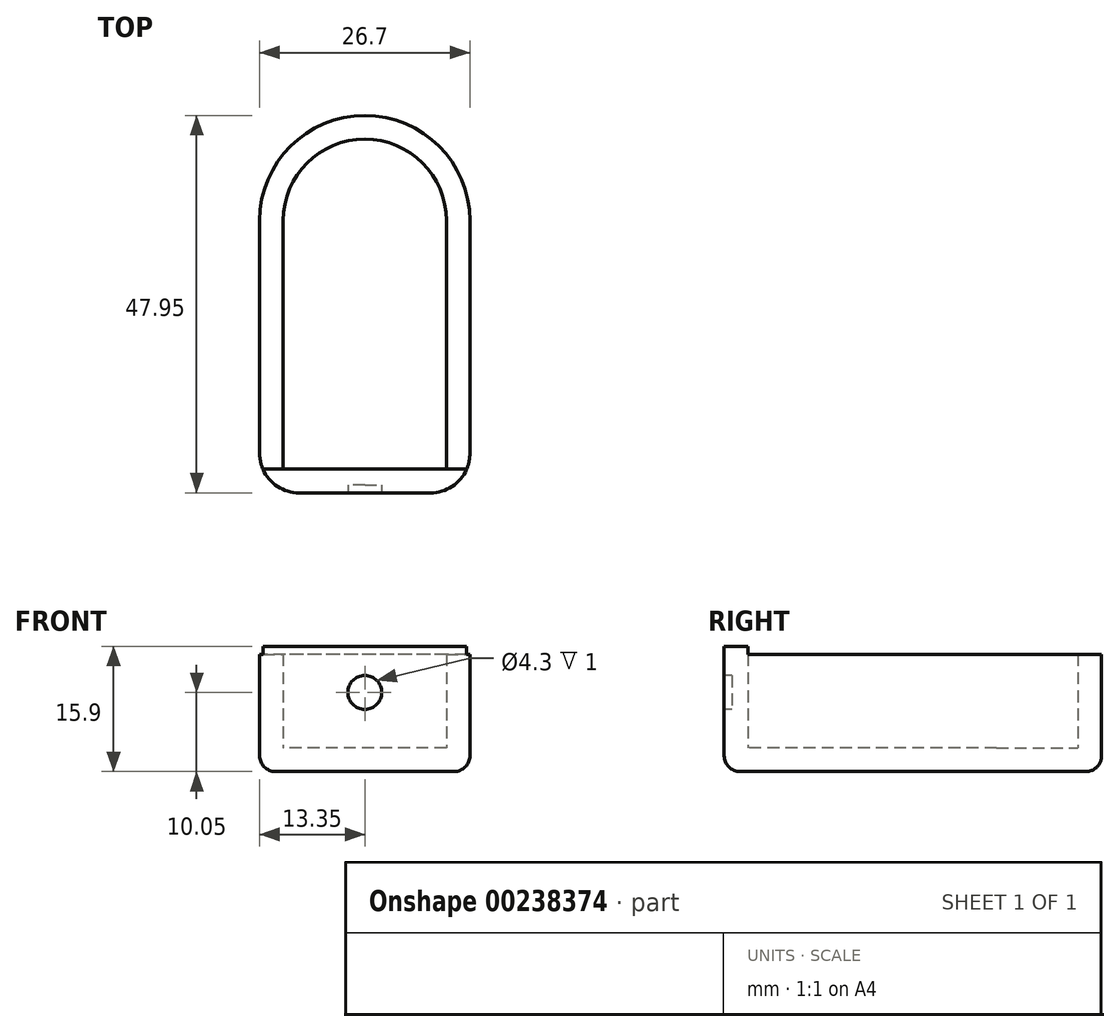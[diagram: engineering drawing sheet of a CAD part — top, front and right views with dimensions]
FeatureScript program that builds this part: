
annotation { "Feature Type Name" : "Feature", "Feature Type Description" : "" }
export const myFeature = defineFeature(function(context is Context, id is Id, definition is map)
    precondition{}
    {
        {
            var Q0;
            Q0=qCreatedBy(makeId("Top.planeOp"),FACE);
            var sketch = newSketch(context, id + "F0", { "sketchPlane" : qUnion([Q0])});
            skArc(sketch, "E0", {"start": v(13.35, 0) * mm, "mid": v(0, 13.35) * mm, "end": v(-13.35, 0) * mm});
            skLineSegment(sketch, "E1", {"start": v(-13.35, 0) * mm, "end": v(-13.35, -34.6) * mm});
            skLineSegment(sketch, "E2", {"start": v(13.35, 0) * mm, "end": v(13.35, -34.6) * mm});
            skLineSegment(sketch, "E3", {"start": v(13.35, -34.6) * mm, "end": v(-13.35, -34.6) * mm});
            skPoint(sketch, "E4.orphan", {"position": v(0, -34.6) * mm});
            skPoint(sketch, "E5.end.orphan", {"position": v(0, 13.35) * mm});
            skLineSegment(sketch, "E6.0", {"start": v(-10.35, 0) * mm, "end": v(-10.35, -31.6) * mm});
            skArc(sketch, "E6.1", {"start": v(10.35, 0) * mm, "mid": v(0, 10.35) * mm, "end": v(-10.35, 0) * mm});
            skLineSegment(sketch, "E6.2", {"start": v(10.35, 0) * mm, "end": v(10.35, -31.6) * mm});
            skLineSegment(sketch, "E6.3", {"start": v(10.35, -31.6) * mm, "end": v(-10.35, -31.6) * mm});
            skSolve(sketch);
        }
        {
            var Q0;
            Q0=makeQuery(id+"F0.imprint","IMPRINT",FACE,{"disambiguationData":[TD([[makeQuery(id+"F0.imprint","IMPRINT",EDGE,{"derivedFrom":sQuery(id+"F0.wireOp",EDGE,"E0")}),1.0]])]});
            var Q1;
            Q1=makeQuery(id+"F0.imprint","IMPRINT",FACE,{"disambiguationData":[TD([[makeQuery(id+"F0.imprint","IMPRINT",EDGE,{"derivedFrom":sQuery(id+"F0.wireOp",EDGE,"E6.0")}),1.0]])]});
            extrude(context, id + "F1", {"entities" : qUnion([Q0, Q1]), "oppositeDirection" : true, "depth" : 3 * mm});
        }
        {
            var Q0;
            Q0=makeQuery(id+"F0.imprint","IMPRINT",FACE,{"disambiguationData":[TD([[makeQuery(id+"F0.imprint","IMPRINT",EDGE,{"derivedFrom":sQuery(id+"F0.wireOp",EDGE,"E0")}),1.0]])]});
            extrude(context, id + "F2", {"entities" : qUnion([Q0]), "operationType" : NewBodyOperationType.ADD, "depth" : 11.9 * mm});
        }
        {
            var Q0;
            Q0=makeQuery(id+"F2.opExtrude","CAP_FACE",FACE,{"disambiguationData":[OSD([sQuery(id+"F0.wireOp",EDGE,"E0"),sQuery(id+"F0.wireOp",EDGE,"E1"),sQuery(id+"F0.wireOp",EDGE,"E2"),sQuery(id+"F0.wireOp",EDGE,"E3"),sQuery(id+"F0.wireOp",EDGE,"E6.0"),sQuery(id+"F0.wireOp",EDGE,"E6.1"),sQuery(id+"F0.wireOp",EDGE,"E6.2"),sQuery(id+"F0.wireOp",EDGE,"E6.3")])],"isStart":false});
            var sketch = newSketch(context, id + "F3", { "sketchPlane" : qUnion([Q0])});
            skLineSegment(sketch, "E7.0", {"start": v(13.35, -34.6) * mm, "end": v(-13.35, -34.6) * mm});
            skLineSegment(sketch, "E8", {"start": v(-13.35, -34.6) * mm, "end": v(-13.35, -31.6) * mm});
            skLineSegment(sketch, "E9", {"start": v(-13.35, -31.6) * mm, "end": v(13.35, -31.6) * mm});
            skLineSegment(sketch, "E10", {"start": v(13.35, -31.6) * mm, "end": v(13.35, -34.6) * mm});
            skSolve(sketch);
        }
        {
            var Q0;
            Q0=makeQuery(id+"F3.imprint","IMPRINT",FACE,{"disambiguationData":[TD([[makeQuery(id+"F3.imprint","IMPRINT",EDGE,{"derivedFrom":sQuery(id+"F3.wireOp",EDGE,"E7.0")}),-1.0]])]});
            extrude(context, id + "F4", {"entities" : qUnion([Q0]), "operationType" : NewBodyOperationType.ADD, "depth" : 1 * mm});
        }
        {
            var Q0;
            {var subQ0=sQuery(id+"F0.wireOp",EDGE,"E3");Q0=makeQuery(id+"F4.boolean.opBoolean","MERGE",FACE,{"derivedFrom":[makeQuery(id+"F2.boolean.opBoolean","MERGE",FACE,{"derivedFrom":[makeQuery(id+"F1.opExtrude","SWEPT_FACE",FACE,{"disambiguationData":[OSD([subQ0])]}),makeQuery(id+"F2.opExtrude","SWEPT_FACE",FACE,{"disambiguationData":[OSD([subQ0])]})]}),makeQuery(id+"F4.opExtrude","SWEPT_FACE",FACE,{"disambiguationData":[OSD([sQuery(id+"F3.wireOp",EDGE,"E7.0")])]})]});}
            var sketch = newSketch(context, id + "F5", { "sketchPlane" : qUnion([Q0])});
            skLineSegment(sketch, "E11.0", {"start": v(13.35, -3) * mm, "end": v(-13.35, -3) * mm});
            skLineSegment(sketch, "E12", {"start": v(-13.35, 4.9) * mm, "end": v(13.35, 4.9) * mm});
            skLineSegment(sketch, "E13", {"start": v(-13.35, 9.2) * mm, "end": v(13.35, 9.2) * mm});
            skLineSegment(sketch, "E14", {"start": v(0, 9.2) * mm, "end": v(0, 4.9) * mm});
            skCircle(sketch, "E15", {"center": v(0, 7.05) * mm, "radius": 2.15 * mm});
            skSolve(sketch);
        }
        {
            var Q0;
            {var subQ0=sQuery(id+"F5.wireOp",EDGE,"E14");Q0=makeQuery(id+"F5.imprint","IMPRINT",FACE,{"disambiguationData":[TD([[makeQuery(id+"F5.imprint","IMPRINT",EDGE,{"derivedFrom":subQ0}),-1.0]])]});}
            var Q1;
            {var subQ0=sQuery(id+"F5.wireOp",EDGE,"E14");Q1=makeQuery(id+"F5.imprint","IMPRINT",FACE,{"disambiguationData":[TD([[makeQuery(id+"F5.imprint","IMPRINT",EDGE,{"derivedFrom":subQ0}),1.0]])]});}
            extrude(context, id + "F6", {"entities" : qUnion([Q0, Q1]), "operationType" : NewBodyOperationType.REMOVE, "oppositeDirection" : true, "depth" : 6 * mm});
        }
        {
            var Q0;
            {var subQ0=sQuery(id+"F0.wireOp",EDGE,"E3");var subQ1=sQuery(id+"F0.wireOp",EDGE,"E1");Q0=makeQuery(id+"F4.boolean.opBoolean","MERGE",EDGE,{"derivedFrom":[makeQuery(id+"F2.boolean.opBoolean","MERGE",EDGE,{"derivedFrom":[makeQuery(id+"F1.opExtrude","SWEPT_EDGE",EDGE,{"disambiguationData":[OSD([subQ1,subQ0])]}),makeQuery(id+"F2.opExtrude","SWEPT_EDGE",EDGE,{"disambiguationData":[OSD([subQ1,subQ0])]})]}),makeQuery(id+"F4.opExtrude","SWEPT_EDGE",EDGE,{"disambiguationData":[OSD([sQuery(id+"F3.wireOp",EDGE,"E7.0"),sQuery(id+"F3.wireOp",EDGE,"E8")])]})]});}
            var Q1;
            {var subQ0=sQuery(id+"F0.wireOp",EDGE,"E3");var subQ1=sQuery(id+"F0.wireOp",EDGE,"E2");Q1=makeQuery(id+"F4.boolean.opBoolean","MERGE",EDGE,{"derivedFrom":[makeQuery(id+"F2.boolean.opBoolean","MERGE",EDGE,{"derivedFrom":[makeQuery(id+"F1.opExtrude","SWEPT_EDGE",EDGE,{"disambiguationData":[OSD([subQ1,subQ0])]}),makeQuery(id+"F2.opExtrude","SWEPT_EDGE",EDGE,{"disambiguationData":[OSD([subQ1,subQ0])]})]}),makeQuery(id+"F4.opExtrude","SWEPT_EDGE",EDGE,{"disambiguationData":[OSD([sQuery(id+"F3.wireOp",EDGE,"E7.0"),sQuery(id+"F3.wireOp",EDGE,"E10")])]})]});}
            fillet(context, id + "F7", {"entities" : qUnion([Q0, Q1]), "radius" : 5 * mm, "tangentPropagation" : true, "allowEdgeOverflow" : false});
        }
        {
            var Q0;
            Q0=makeQuery(id+"F1.opExtrude","CAP_EDGE",EDGE,{"disambiguationData":[OSD([sQuery(id+"F0.wireOp",EDGE,"E2")])],"isStart":false});
            fillet(context, id + "F8", {"entities" : qUnion([Q0]), "radius" : 2 * mm, "tangentPropagation" : true, "allowEdgeOverflow" : false});
        }
        {
            var Q0;
            Q0=makeQuery(id+"F4.boolean.opBoolean","MERGE",FACE,{"derivedFrom":[makeQuery(id+"F2.opExtrude","SWEPT_FACE",FACE,{"disambiguationData":[OSD([sQuery(id+"F0.wireOp",EDGE,"E6.3")])]}),makeQuery(id+"F4.opExtrude","SWEPT_FACE",FACE,{"disambiguationData":[OSD([sQuery(id+"F3.wireOp",EDGE,"E9")])]})]});
            var sketch = newSketch(context, id + "F9", { "sketchPlane" : qUnion([Q0])});
            skCircle(sketch, "E16", {"center": v(0, 7.05) * mm, "radius": 3.53 * mm});
            skSolve(sketch);
        }
        {
            var Q0;
            Q0 = qSketchRegion(id + "F9", true);
            extrude(context, id + "F10", {"entities" : qUnion([Q0]), "operationType" : NewBodyOperationType.ADD, "oppositeDirection" : true, "depth" : 1 * mm});
        }
        {
            var Q0;
            Q0=makeQuery(id+"F10.opExtrude","CAP_FACE",FACE,{"disambiguationData":[OSD([sQuery(id+"F9.wireOp",EDGE,"E16")])],"isStart":false});
            extrude(context, id + "F11", {"entities" : qUnion([Q0]), "operationType" : NewBodyOperationType.ADD, "depth" : 1 * mm});
        }
    });
